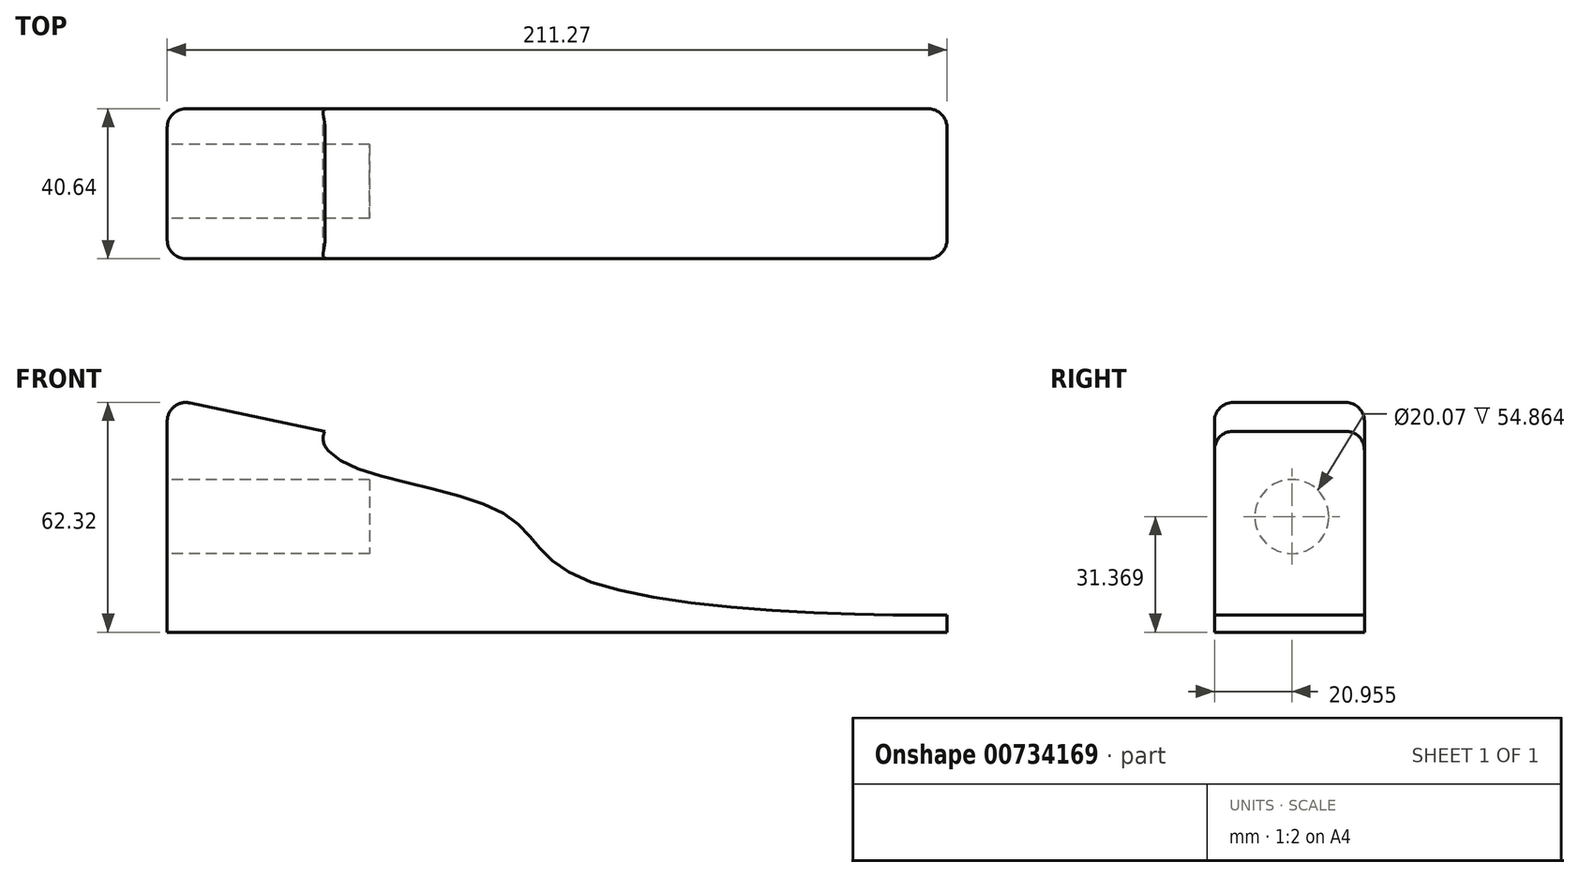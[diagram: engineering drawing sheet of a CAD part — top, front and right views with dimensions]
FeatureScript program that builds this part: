
annotation { "Feature Type Name" : "Feature", "Feature Type Description" : "" }
export const myFeature = defineFeature(function(context is Context, id is Id, definition is map)
    precondition{}
    {
        {
            var Q0;
            Q0=qCreatedBy(makeId("Front.planeOp"),FACE);
            var sketch = newSketch(context, id + "F0", { "sketchPlane" : qUnion([Q0])});
            skLineSegment(sketch, "E0", {"start": v(0, 0) * mm, "end": v(0, 63.5) * mm});
            skLineSegment(sketch, "E1", {"start": v(0, 63.5) * mm, "end": v(211.27, 19.05) * mm});
            skLineSegment(sketch, "E2", {"start": v(211.27, 19.05) * mm, "end": v(211.27, 0) * mm});
            skLineSegment(sketch, "E3", {"start": v(211.27, 0) * mm, "end": v(0, 0) * mm});
            skSolve(sketch);
        }
        {
            var Q0;
            Q0=makeQuery(id+"F0.imprint","IMPRINT",FACE,{"disambiguationData":[TD([[makeQuery(id+"F0.imprint","IMPRINT",EDGE,{"derivedFrom":sQuery(id+"F0.wireOp",EDGE,"E0")}),-1.0]])]});
            extrude(context, id + "F1", {"entities" : qUnion([Q0]), "oppositeDirection" : true, "depth" : 40.64 * mm, "offsetDistance" : 25.4 * mm});
        }
        {
            var Q0;
            Q0=makeQuery(id+"F1.opExtrude","SWEPT_FACE",FACE,{"disambiguationData":[OSD([sQuery(id+"F0.wireOp",EDGE,"E0")])]});
            var sketch = newSketch(context, id + "F2", { "sketchPlane" : qUnion([Q0])});
            skCircle(sketch, "E4", {"center": v(-20.96, 31.37) * mm, "radius": 10.03 * mm});
            skSolve(sketch);
        }
        {
            var Q0;
            Q0=makeQuery(id+"F2.imprint","IMPRINT",FACE,{"disambiguationData":[TD([[makeQuery(id+"F2.imprint","IMPRINT",EDGE,{"derivedFrom":sQuery(id+"F2.wireOp",EDGE,"E4")}),1.0]])]});
            extrude(context, id + "F3", {"entities" : qUnion([Q0]), "operationType" : NewBodyOperationType.REMOVE, "oppositeDirection" : true, "depth" : 54.86 * mm, "offsetDistance" : 25.4 * mm});
        }
        {
            var Q0;
            Q0=makeQuery(id+"F1.opExtrude","CAP_FACE",FACE,{"disambiguationData":[OSD([sQuery(id+"F0.wireOp",EDGE,"E0"),sQuery(id+"F0.wireOp",EDGE,"E1"),sQuery(id+"F0.wireOp",EDGE,"E2"),sQuery(id+"F0.wireOp",EDGE,"E3")])],"isStart":true});
            var sketch = newSketch(context, id + "F4", { "sketchPlane" : qUnion([Q0])});
            skPoint(sketch, "E5.5.internal.snap0", {"position": v(211.27, 9.52) * mm});
            skFitSpline(sketch, "E5", {"points": [v(42.72, 54.51) * mm, v(46.84, 46.6) * mm, v(91.29, 32.13) * mm, v(109.57, 15.88) * mm, v(211.27, 4.7) * mm, v(233.53, 9.52) * mm, v(208.13, 33.4) * mm, v(79.1, 60.83) * mm, v(42.72, 54.51) * mm]});
            skSolve(sketch);
        }
        {
            var Q0;
            {var subQ0=sQuery(id+"F4.wireOp",EDGE,"E5");var subQ1=makeQuery(id+"F1.opExtrude","CAP_EDGE",EDGE,{"disambiguationData":[OSD([sQuery(id+"F0.wireOp",EDGE,"E1")])],"isStart":true});var subQ2=makeQuery(id+"F4.imprint","INTERSECT",VERTEX,{"derivedFrom":[subQ1,subQ0]});Q0=makeQuery(id+"F4.imprint","IMPRINT",FACE,{"disambiguationData":[TD([[makeQuery(id+"F4.imprint","IMPRINT",EDGE,{"disambiguationData":[TD([[subQ2,1.0]])],"derivedFrom":subQ0}),1.0]])]});}
            var Q1;
            {var subQ0=sQuery(id+"F4.wireOp",EDGE,"E5");var subQ1=makeQuery(id+"F1.opExtrude","CAP_EDGE",EDGE,{"disambiguationData":[OSD([sQuery(id+"F0.wireOp",EDGE,"E1")])],"isStart":true});var subQ2=makeQuery(id+"F4.imprint","INTERSECT",VERTEX,{"derivedFrom":[subQ1,subQ0]});Q1=makeQuery(id+"F4.imprint","IMPRINT",FACE,{"disambiguationData":[TD([[makeQuery(id+"F4.imprint","IMPRINT",EDGE,{"disambiguationData":[TD([[subQ2,-1.0]])],"derivedFrom":subQ0}),1.0]])]});}
            extrude(context, id + "F5", {"entities" : qUnion([Q0, Q1]), "operationType" : NewBodyOperationType.REMOVE, "oppositeDirection" : true, "depth" : 50.8 * mm, "offsetDistance" : 25.4 * mm});
        }
        {
            var Q0;
            Q0=makeQuery(id+"F1.opExtrude","CAP_EDGE",EDGE,{"disambiguationData":[OSD([sQuery(id+"F0.wireOp",EDGE,"E1")])],"isStart":true});
            fillet(context, id + "F6", {"entities" : qUnion([Q0]), "radius" : 5.08 * mm, "tangentPropagation" : true, "allowEdgeOverflow" : false});
        }
        {
            var Q0;
            Q0=makeQuery(id+"F1.opExtrude","CAP_EDGE",EDGE,{"disambiguationData":[OSD([sQuery(id+"F0.wireOp",EDGE,"E2")])],"isStart":true});
            fillet(context, id + "F7", {"entities" : qUnion([Q0]), "radius" : 5.08 * mm, "tangentPropagation" : true, "allowEdgeOverflow" : false});
        }
        {
            var Q0;
            Q0=makeQuery(id+"F1.opExtrude","CAP_EDGE",EDGE,{"disambiguationData":[OSD([sQuery(id+"F0.wireOp",EDGE,"E2")])],"isStart":false});
            fillet(context, id + "F8", {"entities" : qUnion([Q0]), "radius" : 5.08 * mm, "tangentPropagation" : true, "allowEdgeOverflow" : false});
        }
        {
            var Q0;
            Q0=makeQuery(id+"F1.opExtrude","CAP_EDGE",EDGE,{"disambiguationData":[OSD([sQuery(id+"F0.wireOp",EDGE,"E1")])],"isStart":false});
            fillet(context, id + "F9", {"entities" : qUnion([Q0]), "radius" : 5.08 * mm, "tangentPropagation" : true, "allowEdgeOverflow" : false});
        }
        {
            var Q0;
            Q0=makeQuery(id+"F1.opExtrude","CAP_EDGE",EDGE,{"disambiguationData":[OSD([sQuery(id+"F0.wireOp",EDGE,"E0")])],"isStart":true});
            fillet(context, id + "F10", {"entities" : qUnion([Q0]), "radius" : 5.08 * mm, "tangentPropagation" : true, "allowEdgeOverflow" : false});
        }
    });
